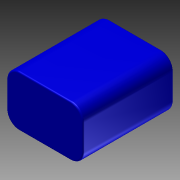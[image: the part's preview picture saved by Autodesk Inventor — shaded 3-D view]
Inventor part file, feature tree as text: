
AUTODESK INVENTOR PART (.ipt)
format: ipt  version: 2013 (Build 170138000, 138)  size: 105,472 bytes
history: native  units: in
note: dims shown in document units (in); Inventor stores cm internally (conversion verified against a paired STEP export)
features: fillet x2, extrude x1, sketch x1
ambient origin geometry x8: Origin, YZ Plane, XZ Plane, XY Plane, X Axis, Y Axis, Z Axis, Center Point
bodies: Solid1 (feature_tree)
feature tree (4):
  extrude  "Extrusion1"  Depth=1.125in
  fillet  "Fillet1"  Radius=2.0in
  fillet  "Fillet2"  Radius=0.281in
  sketch  "Sketch1"  dims[d0=1.688in d1=1.125in d2=2.0in d3=0.0in d4=0.281in d5=0.032in]
